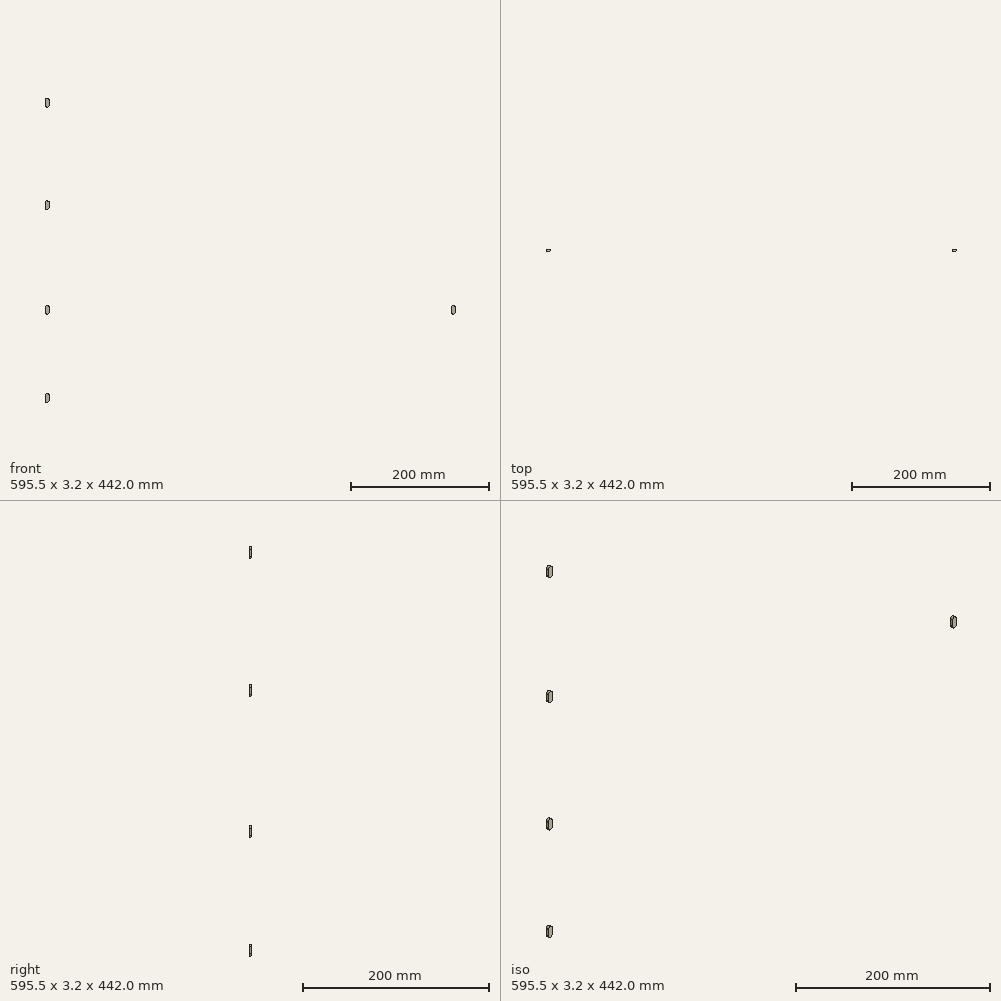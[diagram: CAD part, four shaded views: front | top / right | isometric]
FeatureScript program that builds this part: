
annotation { "Feature Type Name" : "Feature", "Feature Type Description" : "" }
export const myFeature = defineFeature(function(context is Context, id is Id, definition is map)
    precondition{}
    {
        {
            var Q0;
            Q0=qCreatedBy(makeId("Front.planeOp"),FACE);
            var sketch = newSketch(context, id + "F0", { "sketchPlane" : qUnion([Q0])});
            skLineSegment(sketch, "E0.bottom", {"start": v(583, 248.5) * mm, "end": v(-583, 248.5) * mm});
            skLineSegment(sketch, "E0.top", {"start": v(583, -248.5) * mm, "end": v(-583, -248.5) * mm});
            skLineSegment(sketch, "E0.left", {"start": v(583, 248.5) * mm, "end": v(583, -248.5) * mm});
            skLineSegment(sketch, "E0.right", {"start": v(-583, 248.5) * mm, "end": v(-583, -248.5) * mm});
            skPoint(sketch, "E0.middle", {"position": v(0, 0) * mm});
            skSolve(sketch);
        }
        {
            var Q0;
            Q0=makeQuery(id+"F0.imprint","IMPRINT",FACE,{"disambiguationData":[TD([[makeQuery(id+"F0.imprint","IMPRINT",EDGE,{"derivedFrom":sQuery(id+"F0.wireOp",EDGE,"E0.bottom")}),1.0]])]});
            extrude(context, id + "F1", {"entities" : qUnion([Q0]), "depth" : 3.17 * mm, "offsetDistance" : 25 * mm});
        }
        {
            var Q0;
            Q0=makeQuery(id+"F0.imprint","IMPRINT",FACE,{"disambiguationData":[TD([[makeQuery(id+"F0.imprint","IMPRINT",EDGE,{"derivedFrom":sQuery(id+"F0.wireOp",EDGE,"E0.bottom")}),1.0]])]});
            var sketch = newSketch(context, id + "F2", { "sketchPlane" : qUnion([Q0])});
            skPoint(sketch, "E1", {"position": v(-295, 235.5) * mm});
            skPoint(sketch, "E2", {"position": v(-295, 86.5) * mm});
            skPoint(sketch, "E3", {"position": v(-295, -65.5) * mm});
            skPoint(sketch, "E4", {"position": v(-295, -193.5) * mm});
            skPoint(sketch, "E5", {"position": v(295, 235.5) * mm});
            skPoint(sketch, "E6", {"position": v(295, 86.5) * mm});
            skPoint(sketch, "E7", {"position": v(295, -65.5) * mm});
            skPoint(sketch, "E8", {"position": v(295, -193.5) * mm});
            skLineSegment(sketch, "E9", {"start": v(295, 235.5) * mm, "end": v(295, -193.5) * mm});
            skLineSegment(sketch, "E10", {"start": v(-295, 239.25) * mm, "end": v(-295, 231.75) * mm});
            skArc(sketch, "E11.0.startCap", {"start": v(-297.75, 239.25) * mm, "mid": v(-295, 242) * mm, "end": v(-292.25, 239.25) * mm});
            skArc(sketch, "E11.0.endCap", {"start": v(-292.25, 231.75) * mm, "mid": v(-295, 229) * mm, "end": v(-297.75, 231.75) * mm});
            skLineSegment(sketch, "E11.0.left", {"start": v(-292.25, 239.25) * mm, "end": v(-292.25, 231.75) * mm});
            skLineSegment(sketch, "E11.0.right", {"start": v(-297.75, 239.25) * mm, "end": v(-297.75, 231.75) * mm});
            skLineSegment(sketch, "E12", {"start": v(-295, 90.25) * mm, "end": v(-295, 82.75) * mm});
            skArc(sketch, "E13.0.startCap", {"start": v(-297.75, 90.25) * mm, "mid": v(-295, 93) * mm, "end": v(-292.25, 90.25) * mm});
            skArc(sketch, "E13.0.endCap", {"start": v(-292.25, 82.75) * mm, "mid": v(-295, 80) * mm, "end": v(-297.75, 82.75) * mm});
            skLineSegment(sketch, "E13.0.left", {"start": v(-292.25, 90.25) * mm, "end": v(-292.25, 82.75) * mm});
            skLineSegment(sketch, "E13.0.right", {"start": v(-297.75, 90.25) * mm, "end": v(-297.75, 82.75) * mm});
            skLineSegment(sketch, "E14", {"start": v(-295, -61.75) * mm, "end": v(-295, -69.25) * mm});
            skLineSegment(sketch, "E15", {"start": v(-295, -193.5) * mm, "end": v(-295, -189.75) * mm});
            skLineSegment(sketch, "E16", {"start": v(-295, -189.75) * mm, "end": v(-295, -197.25) * mm});
            skArc(sketch, "E17.0.startCap", {"start": v(-297.75, -61.75) * mm, "mid": v(-295, -59) * mm, "end": v(-292.25, -61.75) * mm});
            skArc(sketch, "E17.0.endCap", {"start": v(-292.25, -69.25) * mm, "mid": v(-295, -72) * mm, "end": v(-297.75, -69.25) * mm});
            skLineSegment(sketch, "E17.0.left", {"start": v(-292.25, -61.75) * mm, "end": v(-292.25, -69.25) * mm});
            skLineSegment(sketch, "E17.0.right", {"start": v(-297.75, -61.75) * mm, "end": v(-297.75, -69.25) * mm});
            skArc(sketch, "E17.1.startCap", {"start": v(-297.75, -189.75) * mm, "mid": v(-295, -187) * mm, "end": v(-292.25, -189.75) * mm});
            skArc(sketch, "E17.1.endCap", {"start": v(-292.25, -197.25) * mm, "mid": v(-295, -200) * mm, "end": v(-297.75, -197.25) * mm});
            skLineSegment(sketch, "E17.1.left", {"start": v(-292.25, -189.75) * mm, "end": v(-292.25, -197.25) * mm});
            skLineSegment(sketch, "E17.1.right", {"start": v(-297.75, -189.75) * mm, "end": v(-297.75, -197.25) * mm});
            skArc(sketch, "E18.MirrorCS", {"start": v(297.75, -189.75) * mm, "mid": v(295, -187) * mm, "end": v(292.25, -189.75) * mm});
            skLineSegment(sketch, "E19.MirrorCS", {"start": v(295, -193.5) * mm, "end": v(295, -189.75) * mm});
            skLineSegment(sketch, "E20.MirrorCS", {"start": v(295, -61.75) * mm, "end": v(295, -69.25) * mm});
            skLineSegment(sketch, "E21.MirrorCS", {"start": v(297.75, 90.25) * mm, "end": v(297.75, 82.75) * mm});
            skArc(sketch, "E22.MirrorCS", {"start": v(292.25, -69.25) * mm, "mid": v(295, -72) * mm, "end": v(297.75, -69.25) * mm});
            skLineSegment(sketch, "E23.MirrorCS", {"start": v(292.25, 90.25) * mm, "end": v(292.25, 82.75) * mm});
            skArc(sketch, "E24.MirrorCS", {"start": v(297.75, 90.25) * mm, "mid": v(295, 93) * mm, "end": v(292.25, 90.25) * mm});
            skLineSegment(sketch, "E25.MirrorCS", {"start": v(295, 90.25) * mm, "end": v(295, 82.75) * mm});
            skLineSegment(sketch, "E26.MirrorCS", {"start": v(295, 239.25) * mm, "end": v(295, 231.75) * mm});
            skLineSegment(sketch, "E27.MirrorCS", {"start": v(292.25, -189.75) * mm, "end": v(292.25, -197.25) * mm});
            skLineSegment(sketch, "E28.MirrorCS", {"start": v(292.25, -61.75) * mm, "end": v(292.25, -69.25) * mm});
            skLineSegment(sketch, "E29.MirrorCS", {"start": v(295, -189.75) * mm, "end": v(295, -197.25) * mm});
            skLineSegment(sketch, "E30.MirrorCS", {"start": v(297.75, -61.75) * mm, "end": v(297.75, -69.25) * mm});
            skLineSegment(sketch, "E31.MirrorCS", {"start": v(297.75, -189.75) * mm, "end": v(297.75, -197.25) * mm});
            skArc(sketch, "E32.MirrorCS", {"start": v(292.25, -197.25) * mm, "mid": v(295, -200) * mm, "end": v(297.75, -197.25) * mm});
            skLineSegment(sketch, "E33.MirrorCS", {"start": v(297.75, 239.25) * mm, "end": v(297.75, 231.75) * mm});
            skArc(sketch, "E34.MirrorCS", {"start": v(292.25, 231.75) * mm, "mid": v(295, 229) * mm, "end": v(297.75, 231.75) * mm});
            skArc(sketch, "E35.MirrorCS", {"start": v(292.25, 82.75) * mm, "mid": v(295, 80) * mm, "end": v(297.75, 82.75) * mm});
            skLineSegment(sketch, "E36.MirrorCS", {"start": v(292.25, 239.25) * mm, "end": v(292.25, 231.75) * mm});
            skArc(sketch, "E37.MirrorCS", {"start": v(297.75, 239.25) * mm, "mid": v(295, 242) * mm, "end": v(292.25, 239.25) * mm});
            skArc(sketch, "E38.MirrorCS", {"start": v(297.75, -61.75) * mm, "mid": v(295, -59) * mm, "end": v(292.25, -61.75) * mm});
            skSolve(sketch);
        }
        {
            var Q0;
            Q0=makeQuery(id+"F2.imprint","IMPRINT",FACE,{"disambiguationData":[TD([[makeQuery(id+"F2.imprint","IMPRINT",EDGE,{"derivedFrom":sQuery(id+"F2.wireOp",EDGE,"E11.0.startCap")}),-1.0]])]});
            var Q1;
            Q1=makeQuery(id+"F2.imprint","IMPRINT",FACE,{"disambiguationData":[TD([[makeQuery(id+"F2.imprint","IMPRINT",EDGE,{"derivedFrom":sQuery(id+"F2.wireOp",EDGE,"E13.0.startCap")}),-1.0]])]});
            var Q2;
            Q2=makeQuery(id+"F2.imprint","IMPRINT",FACE,{"disambiguationData":[TD([[makeQuery(id+"F2.imprint","IMPRINT",EDGE,{"derivedFrom":sQuery(id+"F2.wireOp",EDGE,"E17.0.startCap")}),-1.0]])]});
            var Q3;
            Q3=makeQuery(id+"F2.imprint","IMPRINT",FACE,{"disambiguationData":[TD([[makeQuery(id+"F2.imprint","IMPRINT",EDGE,{"derivedFrom":sQuery(id+"F2.wireOp",EDGE,"E17.1.startCap")}),-1.0]])]});
            var Q4;
            {var subQ1=sQuery(id+"F2.wireOp",EDGE,"E33.MirrorCS");Q4=makeQuery(id+"F2.imprint","IMPRINT",FACE,{"disambiguationData":[TD([[makeQuery(id+"F2.imprint","IMPRINT",EDGE,{"derivedFrom":subQ1}),-1.0]])]});}
            var Q5;
            {var subQ1=sQuery(id+"F2.wireOp",EDGE,"E23.MirrorCS");Q5=makeQuery(id+"F2.imprint","IMPRINT",FACE,{"disambiguationData":[TD([[makeQuery(id+"F2.imprint","IMPRINT",EDGE,{"derivedFrom":subQ1}),1.0]])]});}
            var Q6;
            {var subQ1=sQuery(id+"F2.wireOp",EDGE,"E21.MirrorCS");Q6=makeQuery(id+"F2.imprint","IMPRINT",FACE,{"disambiguationData":[TD([[makeQuery(id+"F2.imprint","IMPRINT",EDGE,{"derivedFrom":subQ1}),-1.0]])]});}
            var Q7;
            {var subQ4=sQuery(id+"F2.wireOp",EDGE,"E20.MirrorCS");Q7=makeQuery(id+"F2.imprint","IMPRINT",FACE,{"disambiguationData":[TD([[makeQuery(id+"F2.imprint","IMPRINT",EDGE,{"derivedFrom":subQ4}),1.0]])]});}
            var Q8;
            {var subQ4=sQuery(id+"F2.wireOp",EDGE,"E20.MirrorCS");Q8=makeQuery(id+"F2.imprint","IMPRINT",FACE,{"disambiguationData":[TD([[makeQuery(id+"F2.imprint","IMPRINT",EDGE,{"derivedFrom":subQ4}),-1.0]])]});}
            var Q9;
            {var subQ1=sQuery(id+"F2.wireOp",EDGE,"E27.MirrorCS");Q9=makeQuery(id+"F2.imprint","IMPRINT",FACE,{"disambiguationData":[TD([[makeQuery(id+"F2.imprint","IMPRINT",EDGE,{"derivedFrom":subQ1}),1.0]])]});}
            extrude(context, id + "F3", {"entities" : qUnion([Q0, Q1, Q2, Q3, Q4, Q5, Q6, Q7, Q8, Q9]), "operationType" : NewBodyOperationType.REMOVE, "depth" : 25 * mm, "offsetDistance" : 25 * mm});
        }
    });
